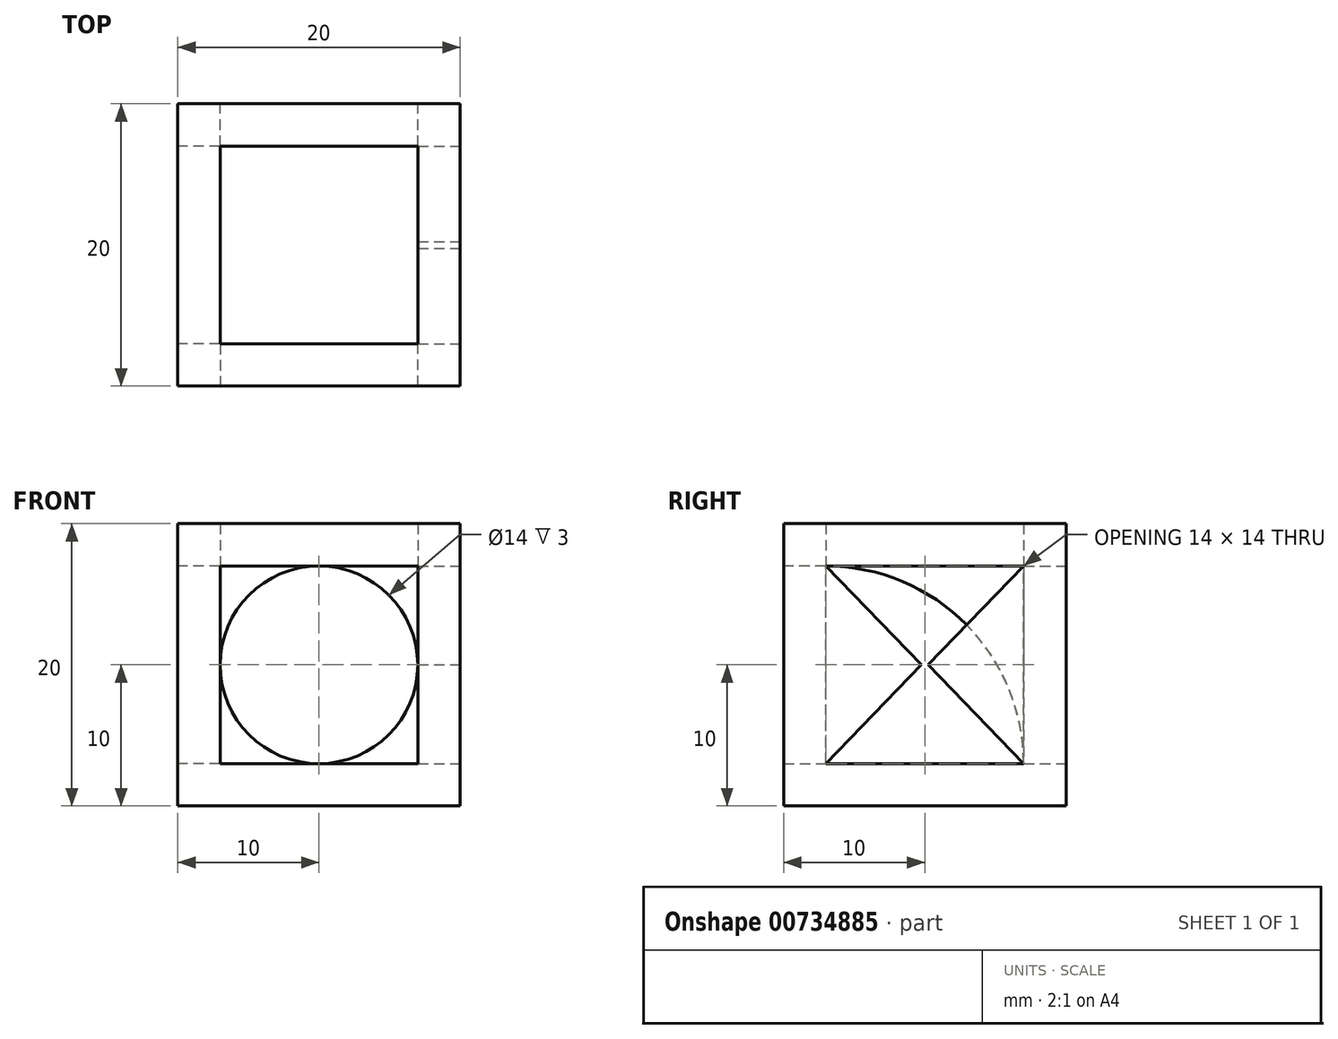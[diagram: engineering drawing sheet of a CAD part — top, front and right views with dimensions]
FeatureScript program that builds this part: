
annotation { "Feature Type Name" : "Feature", "Feature Type Description" : "" }
export const myFeature = defineFeature(function(context is Context, id is Id, definition is map)
    precondition{}
    {
        {
            var Q0;
            Q0=qCreatedBy(makeId("Front.planeOp"),FACE);
            var sketch = newSketch(context, id + "F0", { "sketchPlane" : qUnion([Q0])});
            skLineSegment(sketch, "E0.bottom", {"start": v(-10, 10) * mm, "end": v(10, 10) * mm});
            skLineSegment(sketch, "E0.top", {"start": v(-10, -10) * mm, "end": v(10, -10) * mm});
            skLineSegment(sketch, "E0.left", {"start": v(-10, 10) * mm, "end": v(-10, -10) * mm});
            skLineSegment(sketch, "E0.right", {"start": v(10, 10) * mm, "end": v(10, -10) * mm});
            skSolve(sketch);
        }
        {
            var Q0;
            Q0 = qSketchRegion(id + "F0", true);
            extrude(context, id + "F1", {"entities" : qUnion([Q0]), "endBound" : BoundingType.SYMMETRIC, "depth" : 20 * mm, "offsetDistance" : 25 * mm});
        }
        {
            var Q0;
            Q0=makeQuery(id+"F1.opExtrude","SWEPT_FACE",FACE,{"disambiguationData":[OSD([sQuery(id+"F0.wireOp",EDGE,"E0.bottom")])]});
            shell(context, id + "F2", {"entities" : qUnion([Q0]), "thickness" : 3 * mm});
        }
        {
            var Q0;
            Q0=makeQuery(id+"F1.opExtrude","CAP_FACE",FACE,{"disambiguationData":[OSD([sQuery(id+"F0.wireOp",EDGE,"E0.bottom"),sQuery(id+"F0.wireOp",EDGE,"E0.top"),sQuery(id+"F0.wireOp",EDGE,"E0.left"),sQuery(id+"F0.wireOp",EDGE,"E0.right")])],"isStart":true});
            var sketch = newSketch(context, id + "F3", { "sketchPlane" : qUnion([Q0])});
            skCircle(sketch, "E1", {"center": v(0, 0) * mm, "radius": 7 * mm});
            skSolve(sketch);
        }
        {
            var Q0;
            Q0=makeQuery(id+"F3.imprint","IMPRINT",FACE,{"disambiguationData":[TD([[makeQuery(id+"F3.imprint","IMPRINT",EDGE,{"derivedFrom":sQuery(id+"F3.wireOp",EDGE,"E1")}),1.0]])]});
            extrude(context, id + "F4", {"entities" : qUnion([Q0]), "operationType" : NewBodyOperationType.REMOVE, "oppositeDirection" : true, "depth" : 6 * mm, "offsetDistance" : 25 * mm});
        }
        {
            var Q0;
            Q0=makeQuery(id+"F1.opExtrude","CAP_FACE",FACE,{"disambiguationData":[OSD([sQuery(id+"F0.wireOp",EDGE,"E0.bottom"),sQuery(id+"F0.wireOp",EDGE,"E0.top"),sQuery(id+"F0.wireOp",EDGE,"E0.left"),sQuery(id+"F0.wireOp",EDGE,"E0.right")])],"isStart":false});
            var sketch = newSketch(context, id + "F5", { "sketchPlane" : qUnion([Q0])});
            skLineSegment(sketch, "E2.bottom", {"start": v(-7, 7) * mm, "end": v(7, 7) * mm});
            skLineSegment(sketch, "E2.top", {"start": v(-7, -7) * mm, "end": v(7, -7) * mm});
            skLineSegment(sketch, "E2.left", {"start": v(-7, 7) * mm, "end": v(-7, -7) * mm});
            skLineSegment(sketch, "E2.right", {"start": v(7, 7) * mm, "end": v(7, -7) * mm});
            skSolve(sketch);
        }
        {
            var Q0;
            Q0=makeQuery(id+"F5.imprint","IMPRINT",FACE,{"disambiguationData":[TD([[makeQuery(id+"F5.imprint","IMPRINT",EDGE,{"derivedFrom":sQuery(id+"F5.wireOp",EDGE,"E2.bottom")}),-1.0]])]});
            extrude(context, id + "F6", {"entities" : qUnion([Q0]), "operationType" : NewBodyOperationType.REMOVE, "oppositeDirection" : true, "depth" : 6 * mm, "offsetDistance" : 25 * mm});
        }
        {
            var Q0;
            Q0=makeQuery(id+"F1.opExtrude","SWEPT_FACE",FACE,{"disambiguationData":[OSD([sQuery(id+"F0.wireOp",EDGE,"E0.right")])]});
            var sketch = newSketch(context, id + "F7", { "sketchPlane" : qUnion([Q0])});
            skLineSegment(sketch, "E3", {"start": v(-7, -7) * mm, "end": v(7, -7) * mm});
            skLineSegment(sketch, "E4", {"start": v(7, -7) * mm, "end": v(0.24, 0) * mm});
            skLineSegment(sketch, "E5", {"start": v(0.24, 0) * mm, "end": v(7, 7) * mm});
            skLineSegment(sketch, "E6", {"start": v(7, 7) * mm, "end": v(-7, 7) * mm});
            skLineSegment(sketch, "E7", {"start": v(-7, 7) * mm, "end": v(-0.24, 0) * mm});
            skLineSegment(sketch, "E8", {"start": v(-0.24, 0) * mm, "end": v(-7, -7) * mm});
            skSolve(sketch);
        }
        {
            var Q0;
            Q0=makeQuery(id+"F7.imprint","IMPRINT",FACE,{"disambiguationData":[TD([[makeQuery(id+"F7.imprint","IMPRINT",EDGE,{"derivedFrom":sQuery(id+"F7.wireOp",EDGE,"E5")}),1.0]])]});
            var Q1;
            Q1=makeQuery(id+"F7.imprint","IMPRINT",FACE,{"disambiguationData":[TD([[makeQuery(id+"F7.imprint","IMPRINT",EDGE,{"derivedFrom":sQuery(id+"F7.wireOp",EDGE,"E3")}),1.0]])]});
            extrude(context, id + "F8", {"entities" : qUnion([Q0, Q1]), "operationType" : NewBodyOperationType.REMOVE, "oppositeDirection" : true, "depth" : 6 * mm, "offsetDistance" : 25 * mm});
        }
        {
            var Q0;
            Q0=makeQuery(id+"F1.opExtrude","SWEPT_FACE",FACE,{"disambiguationData":[OSD([sQuery(id+"F0.wireOp",EDGE,"E0.left")])]});
            var sketch = newSketch(context, id + "F9", { "sketchPlane" : qUnion([Q0])});
            skLineSegment(sketch, "E9", {"start": v(-7, -7) * mm, "end": v(7, -7) * mm});
            skLineSegment(sketch, "E10", {"start": v(7, -7) * mm, "end": v(7, 7) * mm});
            skArc(sketch, "E11", {"start": v(7, 7) * mm, "mid": v(-2.9, 2.9) * mm, "end": v(-7, -7) * mm});
            skSolve(sketch);
        }
        {
            var Q0;
            Q0=makeQuery(id+"F9.imprint","IMPRINT",FACE,{"disambiguationData":[TD([[makeQuery(id+"F9.imprint","IMPRINT",EDGE,{"derivedFrom":sQuery(id+"F9.wireOp",EDGE,"E9")}),1.0]])]});
            extrude(context, id + "F10", {"entities" : qUnion([Q0]), "operationType" : NewBodyOperationType.REMOVE, "oppositeDirection" : true, "depth" : 6 * mm, "offsetDistance" : 25 * mm});
        }
    });
